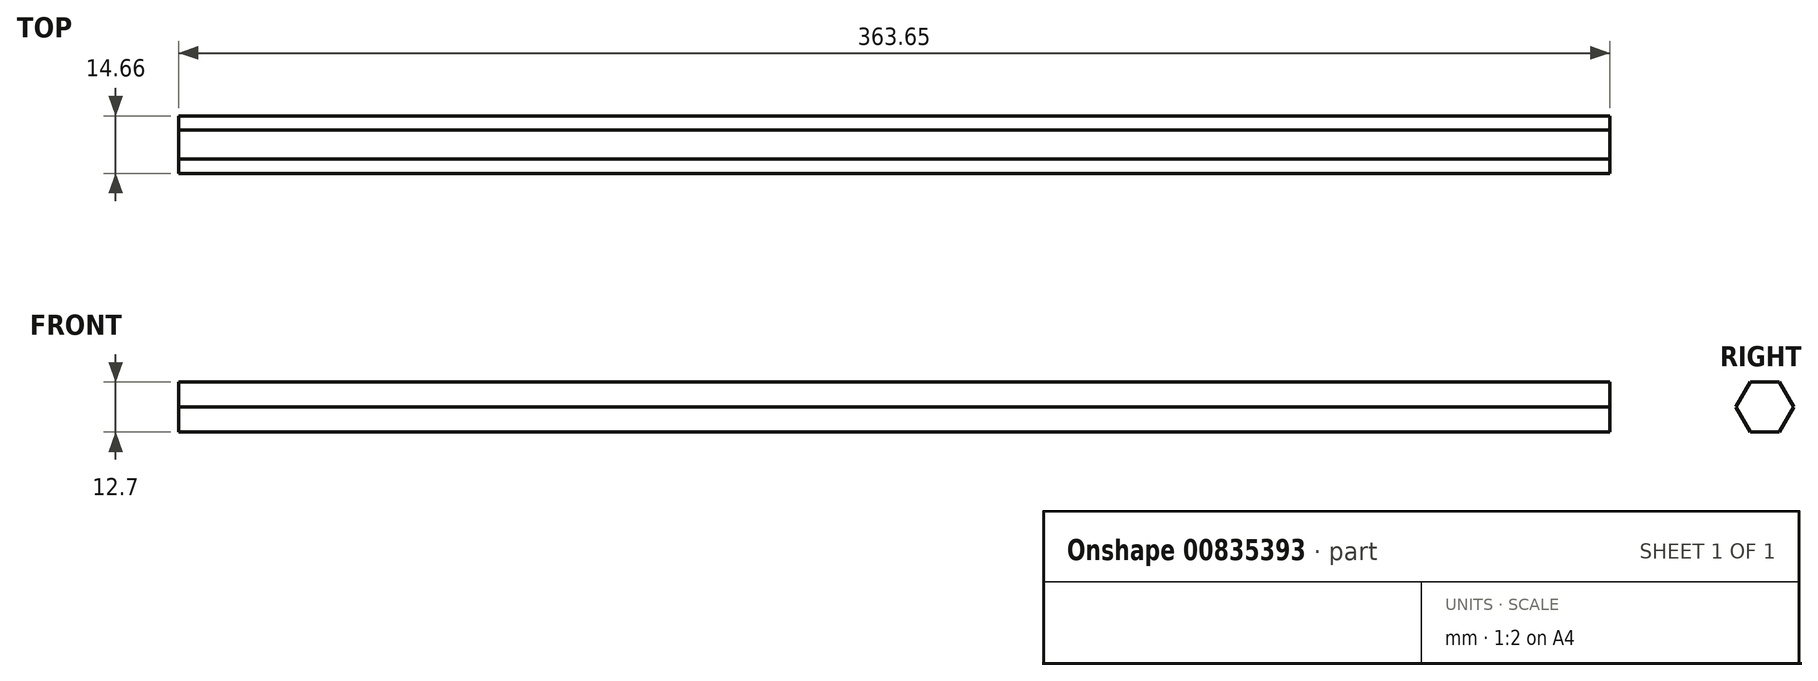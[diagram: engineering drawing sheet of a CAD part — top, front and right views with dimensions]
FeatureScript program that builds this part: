
annotation { "Feature Type Name" : "Feature", "Feature Type Description" : "" }
export const myFeature = defineFeature(function(context is Context, id is Id, definition is map)
    precondition{}
    {
        {
            var Q0;
            Q0=qCreatedBy(makeId("Right.planeOp"),FACE);
            var sketch = newSketch(context, id + "F0", { "sketchPlane" : qUnion([Q0])});
            skCircle(sketch, "E0.cCircle", {"center": v(0, 0) * mm, "radius": 6.35 * mm, "construction": true});
            skLineSegment(sketch, "E0.0", {"start": v(7.33, 0) * mm, "end": v(3.67, -6.35) * mm});
            skLineSegment(sketch, "E0.1", {"start": v(3.67, -6.35) * mm, "end": v(-3.67, -6.35) * mm});
            skLineSegment(sketch, "E0.2", {"start": v(-3.67, -6.35) * mm, "end": v(-7.33, 0) * mm});
            skLineSegment(sketch, "E0.3", {"start": v(-7.33, 0) * mm, "end": v(-3.67, 6.35) * mm});
            skLineSegment(sketch, "E0.4", {"start": v(-3.67, 6.35) * mm, "end": v(3.67, 6.35) * mm});
            skLineSegment(sketch, "E0.5", {"start": v(3.67, 6.35) * mm, "end": v(7.33, 0) * mm});
            skPoint(sketch, "E0.0.midPoint", {"position": v(5.5, -3.18) * mm});
            skLineSegment(sketch, "E1.bottom", {"start": v(6.35, 0) * mm, "end": v(7.33, 0) * mm});
            skSolve(sketch);
        }
        {
            var Q0;
            Q0 = qSketchRegion(id + "F0", true);
            extrude(context, id + "F1", {"entities" : qUnion([Q0]), "depth" : 363.65 * mm, "offsetDistance" : 25.4 * mm});
        }
    });
